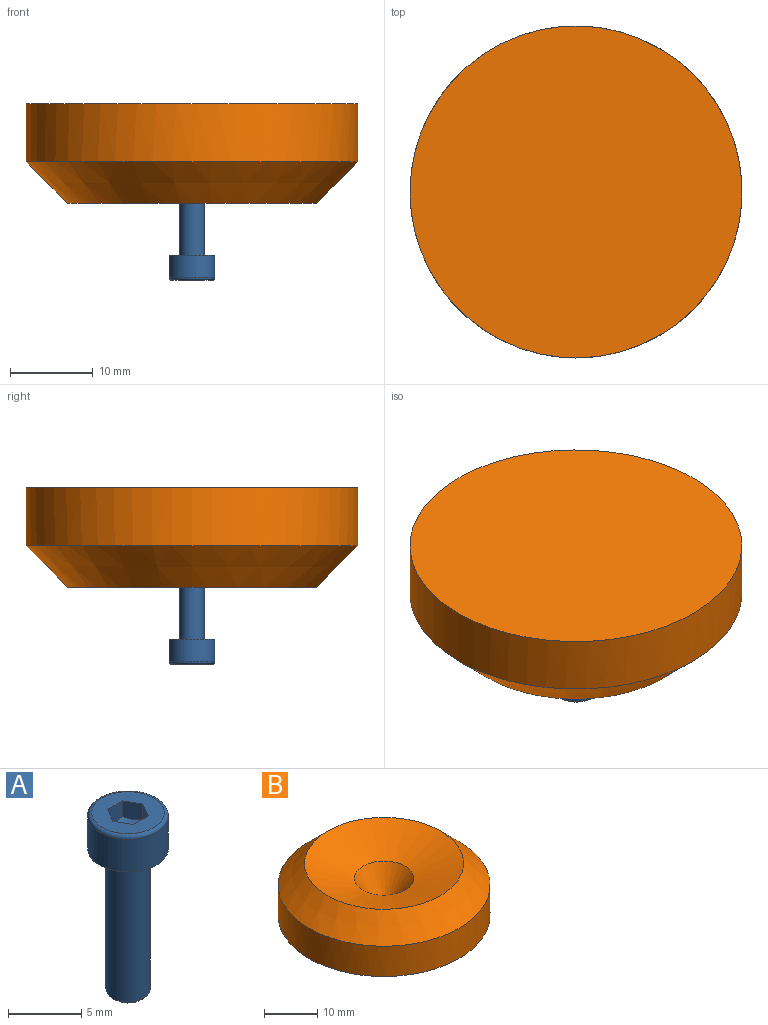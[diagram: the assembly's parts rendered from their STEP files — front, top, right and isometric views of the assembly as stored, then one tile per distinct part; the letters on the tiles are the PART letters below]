
ASSEMBLY  parts=2 mates=1
PART A: 14 faces, bbox 6x6x15 mm
  f0: cylinder r=2.75mm len=5.5mm, axis (0,0,-1), area 47.1mm2, adj f1,f13
  f1: torus R=2.48mm, axis (0,0,-1), area 7.2mm2, adj f0,f12
  f2: cone r=1.36mm half-angle=45deg, axis (0,0,1), area 3.3mm2, adj f3,f11
  f3: cylinder r=1.5mm len=11.73mm, axis (0,0,-1), area 110.5mm2, adj f2,f13
  f4: cone r=0.72mm half-angle=60deg, axis (0,0,1), area 6.2mm2, adj f5,f6,f7,f8,f9,f10
  f5: plane 1.47x1.25mm, normal (0.87,0.5,0), area 2mm2, adj f4,f6,f10,f12
  f6: plane 1.47x1.44mm, normal (0,1,0), area 2mm2, adj f4,f5,f7,f12
  f7: plane 1.47x1.25mm, normal (-0.87,0.5,0), area 2mm2, adj f4,f6,f8,f12
  f8: plane 1.47x1.25mm, normal (-0.87,-0.5,0), area 2mm2, adj f4,f7,f9,f12
  f9: plane 1.44x1.43mm, normal (0,-1,0), area 2mm2, adj f4,f8,f10,f12
  f10: plane 1.47x1.25mm, normal (0.87,-0.5,0), area 2mm2, adj f4,f5,f9,f12
  f11: plane 2.46x2.46mm, normal (0,0,-1), area 4.7mm2, adj f2
  f12: plane 4.95x4.95mm, normal (0,0,1), area 13.8mm2, adj f1,f5,f6,f7,f8,f9,f10
  f13: plane 5.5x5.5mm, normal (0,0,-1), area 16.7mm2, adj f0,f3
PART B: 5 faces, bbox 40x40x12 mm
  f0: cone r=5.59mm half-angle=37.6deg, axis (0,0,1), area 160.9mm2, adj f3
  f1: plane 40x40mm, normal (0,0,-1), area 1256.6mm2, adj f2
  f2: cylinder r=20mm len=40mm, axis (0,0,1), area 879.6mm2, adj f1,f4
  f3: cone r=15mm half-angle=69.9deg, axis (0,0,1), area 647.9mm2, adj f0,f4
  f4: cone r=15mm half-angle=45deg, axis (0,0,-1), area 777.5mm2, adj f2,f3
PLACE A rot(axis=(-0.71,0.71,0),180deg) t=(11.81,-7.11,4.24)mm
PLACE B rot(axis=(0,1,0),180deg) t=(11.81,-7.11,22.49)mm
MATE cylindrical B.f2 <-> A.f4  axis (0,0,1) through (11.81,-7.11,22.49)mm
